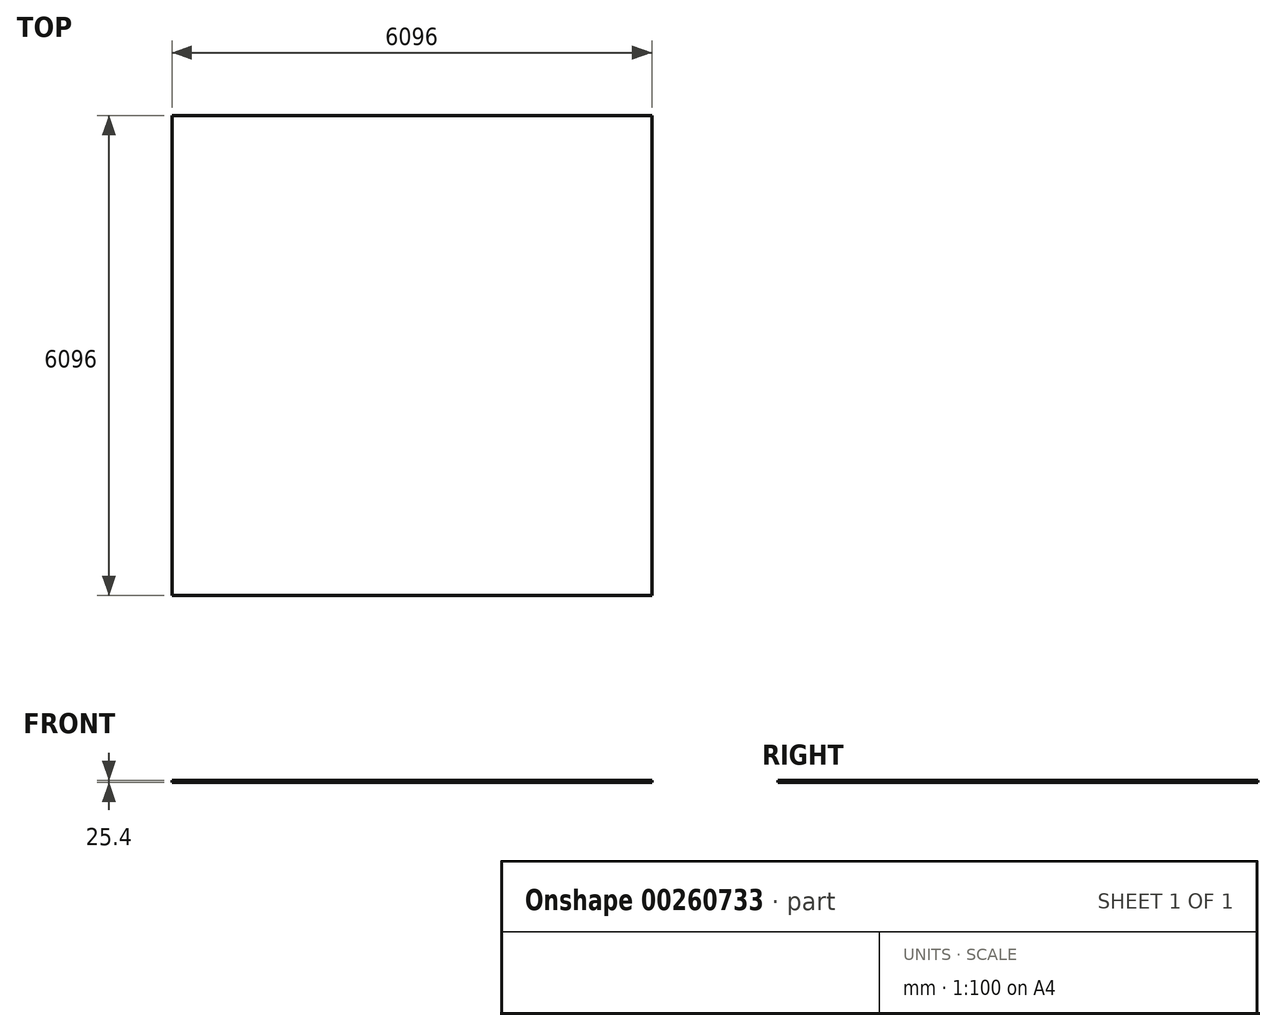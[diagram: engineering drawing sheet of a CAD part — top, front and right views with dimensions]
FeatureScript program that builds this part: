
annotation { "Feature Type Name" : "Feature", "Feature Type Description" : "" }
export const myFeature = defineFeature(function(context is Context, id is Id, definition is map)
    precondition{}
    {
        {
            var Q0;
            Q0=qCreatedBy(makeId("Top.planeOp"),FACE);
            var sketch = newSketch(context, id + "F0", { "sketchPlane" : qUnion([Q0])});
            skLineSegment(sketch, "E0.bottom", {"start": v(3048, 3048) * mm, "end": v(-3048, 3048) * mm});
            skLineSegment(sketch, "E0.top", {"start": v(3048, -3048) * mm, "end": v(-3048, -3048) * mm});
            skLineSegment(sketch, "E0.left", {"start": v(3048, 3048) * mm, "end": v(3048, -3048) * mm});
            skLineSegment(sketch, "E0.right", {"start": v(-3048, 3048) * mm, "end": v(-3048, -3048) * mm});
            skPoint(sketch, "E0.middle", {"position": v(0, 0) * mm});
            skSolve(sketch);
        }
        {
            var Q0;
            Q0=makeQuery(id+"F0.imprint","IMPRINT",FACE,{"disambiguationData":[TD([[makeQuery(id+"F0.imprint","IMPRINT",EDGE,{"derivedFrom":sQuery(id+"F0.wireOp",EDGE,"E0.bottom")}),1.0]])]});
            extrude(context, id + "F1", {"entities" : qUnion([Q0]), "depth" : 25.4 * mm});
        }
    });
